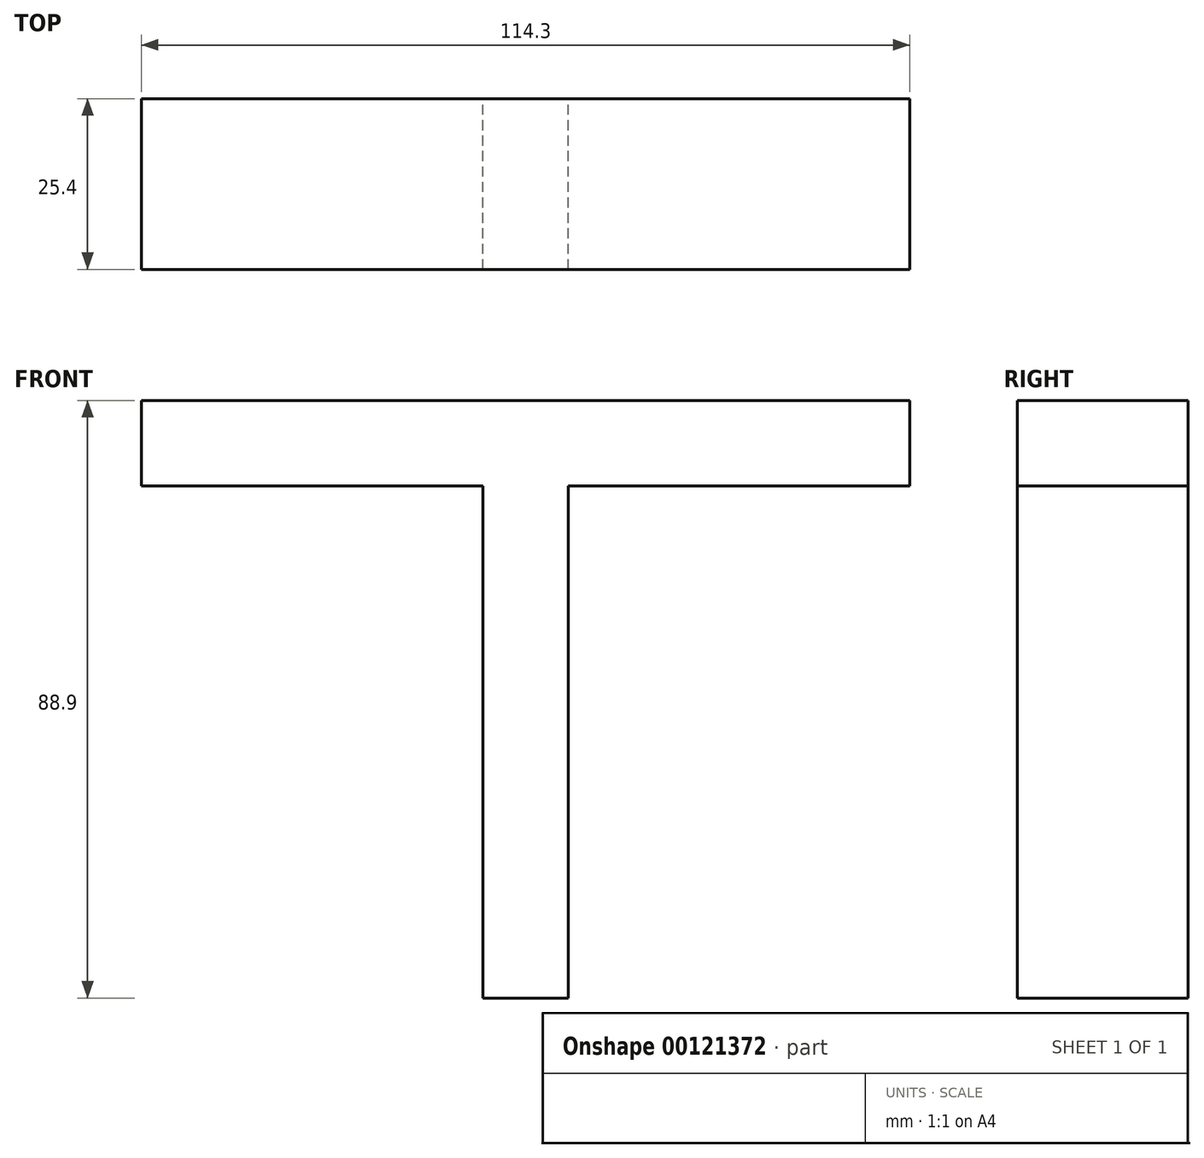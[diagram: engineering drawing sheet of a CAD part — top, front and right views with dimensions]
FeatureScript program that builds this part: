
annotation { "Feature Type Name" : "Feature", "Feature Type Description" : "" }
export const myFeature = defineFeature(function(context is Context, id is Id, definition is map)
    precondition{}
    {
        {
            var Q0;
            Q0=qCreatedBy(makeId("Front.planeOp"),FACE);
            var sketch = newSketch(context, id + "F0", { "sketchPlane" : qUnion([Q0])});
            skLineSegment(sketch, "E0", {"start": v(-63.5, 88.9) * mm, "end": v(-63.5, 76.2) * mm});
            skLineSegment(sketch, "E1", {"start": v(-63.5, 76.2) * mm, "end": v(-12.7, 76.2) * mm});
            skLineSegment(sketch, "E2", {"start": v(-12.7, 76.2) * mm, "end": v(-12.7, 0) * mm});
            skLineSegment(sketch, "E3", {"start": v(-12.7, 0) * mm, "end": v(0, 0) * mm});
            skLineSegment(sketch, "E4", {"start": v(0, 0) * mm, "end": v(0, 76.2) * mm});
            skLineSegment(sketch, "E5", {"start": v(0, 76.2) * mm, "end": v(50.8, 76.2) * mm});
            skLineSegment(sketch, "E6", {"start": v(50.8, 76.2) * mm, "end": v(50.8, 88.9) * mm});
            skLineSegment(sketch, "E7", {"start": v(50.8, 88.9) * mm, "end": v(-63.5, 88.9) * mm});
            skSolve(sketch);
        }
        {
            var Q0;
            Q0=makeQuery(id+"F0.imprint","IMPRINT",FACE,{"disambiguationData":[TD([[makeQuery(id+"F0.imprint","IMPRINT",EDGE,{"derivedFrom":sQuery(id+"F0.wireOp",EDGE,"E0")}),1.0]])]});
            extrude(context, id + "F1", {"entities" : qUnion([Q0]), "depth" : 25.4 * mm});
        }
    });
